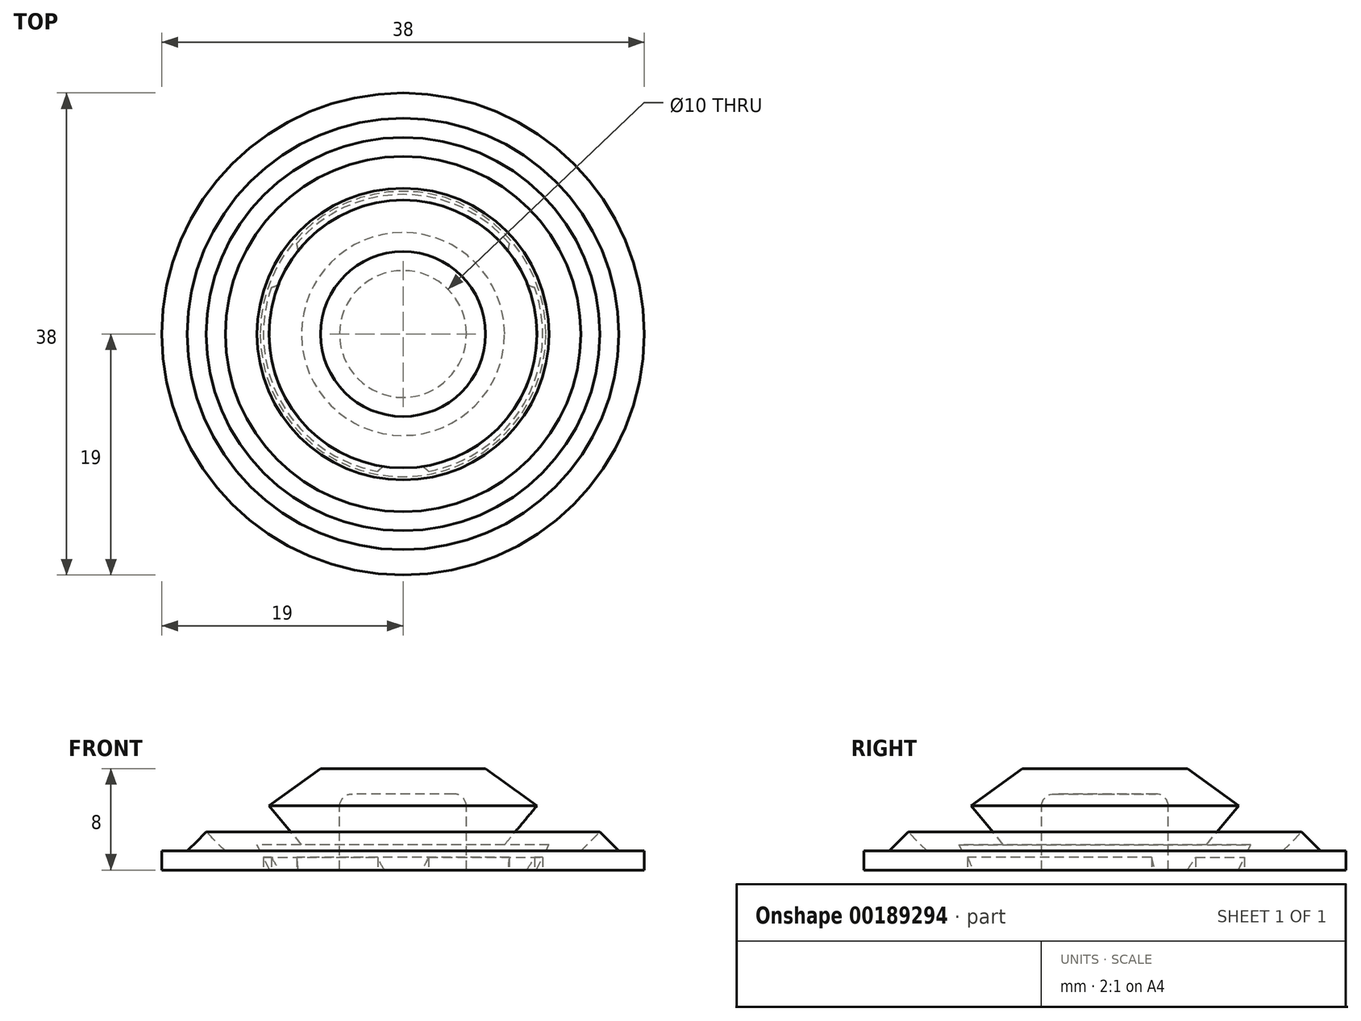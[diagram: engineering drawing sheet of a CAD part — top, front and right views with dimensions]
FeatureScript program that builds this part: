
annotation { "Feature Type Name" : "Feature", "Feature Type Description" : "" }
export const myFeature = defineFeature(function(context is Context, id is Id, definition is map)
    precondition{}
    {
        {
            var Q0;
            Q0=qCreatedBy(makeId("Front.planeOp"),FACE);
            var sketch = newSketch(context, id + "F0", { "sketchPlane" : qUnion([Q0])});
            skLineSegment(sketch, "E0", {"start": v(-10.5, 0) * mm, "end": v(-5, 0) * mm});
            skLineSegment(sketch, "E1", {"start": v(-11.5, 2) * mm, "end": v(-8, 2) * mm});
            skLineSegment(sketch, "E2", {"start": v(-8, 2) * mm, "end": v(-10.56, 5.08) * mm});
            skLineSegment(sketch, "E3", {"start": v(-10.56, 5.08) * mm, "end": v(-6.5, 8) * mm});
            skLineSegment(sketch, "E4", {"start": v(-6.5, 8) * mm, "end": v(0, 8) * mm});
            skLineSegment(sketch, "E5", {"start": v(0, 8) * mm, "end": v(0, 6) * mm});
            skLineSegment(sketch, "E6", {"start": v(0, 6) * mm, "end": v(-4, 6) * mm});
            skLineSegment(sketch, "E7", {"start": v(-5, 5) * mm, "end": v(-5, 0) * mm});
            skPoint(sketch, "E8", {"position": v(-10.5, 0) * mm});
            skLineSegment(sketch, "E9", {"start": v(-10.5, 0) * mm, "end": v(-11.5, 2) * mm});
            skPoint(sketch, "E10", {"position": v(-4, 6) * mm});
            skPoint(sketch, "E11", {"position": v(-5, 5) * mm});
            skArc(sketch, "E12", {"start": v(-4, 6) * mm, "mid": v(-4.7, 5.7) * mm, "end": v(-5, 5) * mm});
            skSolve(sketch);
        }
        {
            var Q0;
            Q0=makeQuery(id+"F0.imprint","IMPRINT",FACE,{"disambiguationData":[TD([[makeQuery(id+"F0.imprint","IMPRINT",EDGE,{"derivedFrom":sQuery(id+"F0.wireOp",EDGE,"E0")}),1.0]])]});
            var Q1;
            Q1=sQuery(id+"F0.wireOp",EDGE,"E5");
            revolve(context, id + "F1", {"entities" : qUnion([Q0]), "axis" : qUnion([Q1]), "revolveType" : RevolveType.FULL});
        }
        {
            var Q0;
            Q0=qCreatedBy(makeId("Front.planeOp"),FACE);
            var sketch = newSketch(context, id + "F2", { "sketchPlane" : qUnion([Q0])});
            skPoint(sketch, "E13", {"position": v(-19, 0) * mm});
            skLineSegment(sketch, "E14", {"start": v(-19, 0) * mm, "end": v(-19, 1.5) * mm});
            skLineSegment(sketch, "E15", {"start": v(-19, 0) * mm, "end": v(-11, 0) * mm});
            skLineSegment(sketch, "E16", {"start": v(-11, 0) * mm, "end": v(-11, 1.5) * mm});
            skLineSegment(sketch, "E17", {"start": v(-11, 1.5) * mm, "end": v(-14, 1.5) * mm});
            skLineSegment(sketch, "E18", {"start": v(-14, 1.5) * mm, "end": v(-15.5, 3) * mm});
            skLineSegment(sketch, "E19", {"start": v(-15.5, 3) * mm, "end": v(-17, 1.5) * mm});
            skLineSegment(sketch, "E20", {"start": v(-17, 1.5) * mm, "end": v(-19, 1.5) * mm});
            skLineSegment(sketch, "E21", {"start": v(0, -2.35) * mm, "end": v(0, 5.58) * mm, "construction": true});
            skLineSegment(sketch, "E22", {"start": v(-11, 1.5) * mm, "end": v(0, 1.5) * mm, "construction": true});
            skSolve(sketch);
        }
        {
            var Q0;
            Q0=makeQuery(id+"F2.imprint","IMPRINT",FACE,{"disambiguationData":[TD([[makeQuery(id+"F2.imprint","IMPRINT",EDGE,{"derivedFrom":sQuery(id+"F2.wireOp",EDGE,"E14")}),-1.0]])]});
            var Q1;
            Q1=sQuery(id+"F2.wireOp",EDGE,"E21");
            revolve(context, id + "F3", {"entities" : qUnion([Q0]), "axis" : qUnion([Q1]), "revolveType" : RevolveType.FULL});
        }
        {
            var Q0;
            Q0=makeQuery(id+"F3.opRevolve","SWEPT_FACE",FACE,{"disambiguationData":[OSD([sQuery(id+"F2.wireOp",EDGE,"E15")])]});
            var sketch = newSketch(context, id + "F4", { "sketchPlane" : qUnion([Q0])});
            skPoint(sketch, "E23", {"position": v(0, 10) * mm});
            skPoint(sketch, "E24", {"position": v(-2, 10.82) * mm});
            skPoint(sketch, "E25", {"position": v(2, 10.82) * mm});
            skLineSegment(sketch, "E26", {"start": v(-2, 10.82) * mm, "end": v(2, 10.82) * mm, "construction": true});
            skPoint(sketch, "E27", {"position": v(0, 10.82) * mm});
            skArc(sketch, "E28", {"start": v(-2, 10.82) * mm, "mid": v(0, 10) * mm, "end": v(2, 10.82) * mm});
            skArc(sketch, "E29", {"start": v(2, 10.82) * mm, "mid": v(0, 11) * mm, "end": v(-2, 10.82) * mm});
            skArc(sketch, "E30.1.0", {"start": v(-8.37, -7.14) * mm, "mid": v(-8.66, -5) * mm, "end": v(-10.37, -3.68) * mm});
            skArc(sketch, "E30.1.1", {"start": v(-10.37, -3.68) * mm, "mid": v(-9.53, -5.5) * mm, "end": v(-8.37, -7.14) * mm});
            skArc(sketch, "E30.2.0", {"start": v(10.37, -3.68) * mm, "mid": v(8.66, -5) * mm, "end": v(8.37, -7.14) * mm});
            skArc(sketch, "E30.2.1", {"start": v(8.37, -7.14) * mm, "mid": v(9.53, -5.5) * mm, "end": v(10.37, -3.68) * mm});
            skSolve(sketch);
        }
        {
            var Q0;
            Q0=makeQuery(id+"F4.imprint","IMPRINT",FACE,{"disambiguationData":[TD([[makeQuery(id+"F4.imprint","IMPRINT",EDGE,{"derivedFrom":sQuery(id+"F4.wireOp",EDGE,"E28")}),1.0]])]});
            var Q1;
            Q1=makeQuery(id+"F4.imprint","IMPRINT",FACE,{"disambiguationData":[TD([[makeQuery(id+"F4.imprint","IMPRINT",EDGE,{"derivedFrom":sQuery(id+"F4.wireOp",EDGE,"E30.1.0")}),1.0]])]});
            var Q2;
            Q2=makeQuery(id+"F4.imprint","IMPRINT",FACE,{"disambiguationData":[TD([[makeQuery(id+"F4.imprint","IMPRINT",EDGE,{"derivedFrom":sQuery(id+"F4.wireOp",EDGE,"E30.2.0")}),1.0]])]});
            var Q3;
            Q3=makeQuery(id+"F3.opRevolve","SWEPT_FACE",FACE,{"disambiguationData":[OSD([sQuery(id+"F2.wireOp",EDGE,"E17")])]});
            extrude(context, id + "F5", {"entities" : qUnion([Q0, Q1, Q2]), "operationType" : NewBodyOperationType.ADD, "endBound" : BoundingType.UP_TO_SURFACE, "oppositeDirection" : true, "depth" : 25 * mm, "endBoundEntityFace" : qUnion([Q3]), "offsetDistance" : 25 * mm});
        }
    });
